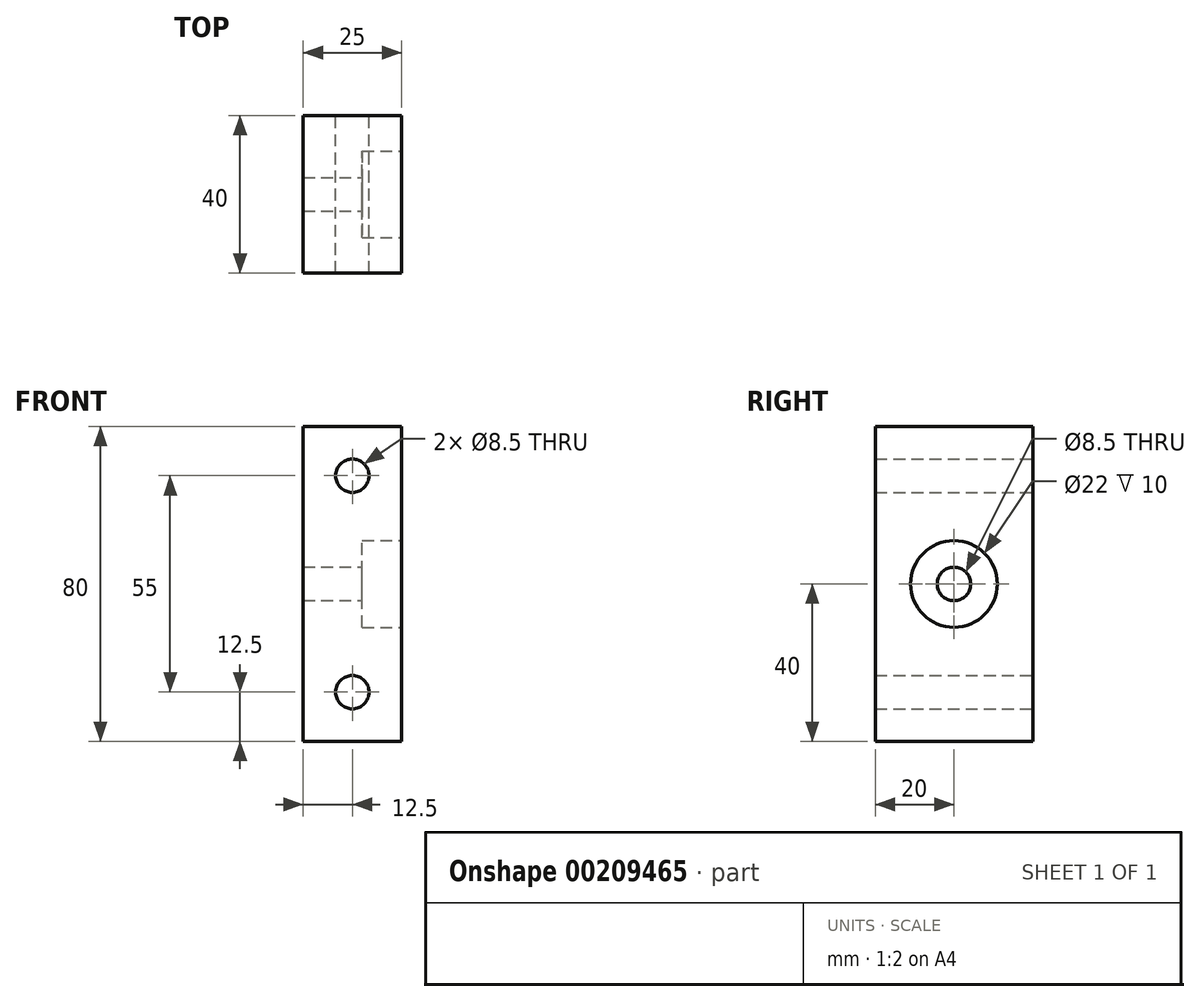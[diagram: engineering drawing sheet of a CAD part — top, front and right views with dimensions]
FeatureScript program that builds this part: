
annotation { "Feature Type Name" : "Feature", "Feature Type Description" : "" }
export const myFeature = defineFeature(function(context is Context, id is Id, definition is map)
    precondition{}
    {
        {
            var Q0;
            Q0=qCreatedBy(makeId("Front.planeOp"),FACE);
            var sketch = newSketch(context, id + "F0", { "sketchPlane" : qUnion([Q0])});
            skLineSegment(sketch, "E0.bottom", {"start": v(12.5, 40) * mm, "end": v(-12.5, 40) * mm});
            skLineSegment(sketch, "E0.top", {"start": v(12.5, -40) * mm, "end": v(-12.5, -40) * mm});
            skLineSegment(sketch, "E0.left", {"start": v(12.5, 40) * mm, "end": v(12.5, -40) * mm});
            skLineSegment(sketch, "E0.right", {"start": v(-12.5, 40) * mm, "end": v(-12.5, -40) * mm});
            skPoint(sketch, "E0.middle", {"position": v(0, 0) * mm});
            skCircle(sketch, "E1", {"center": v(0, 27.5) * mm, "radius": 4.25 * mm});
            skCircle(sketch, "E2", {"center": v(0, -27.5) * mm, "radius": 4.25 * mm});
            skSolve(sketch);
        }
        {
            var Q0;
            Q0 = qSketchRegion(id + "F0", true);
            extrude(context, id + "F1", {"entities" : qUnion([Q0]), "depth" : 20 * mm, "hasSecondDirection" : true, "secondDirectionOppositeDirection" : true, "secondDirectionDepth" : 20 * mm});
        }
        {
            var Q0;
            Q0=qCreatedBy(makeId("Right.planeOp"),FACE);
            var sketch = newSketch(context, id + "F2", { "sketchPlane" : qUnion([Q0])});
            skCircle(sketch, "E3", {"center": v(0, 0) * mm, "radius": 4.25 * mm});
            skSolve(sketch);
        }
        {
            var Q0;
            Q0 = qSketchRegion(id + "F2", true);
            extrude(context, id + "F3", {"entities" : qUnion([Q0]), "operationType" : NewBodyOperationType.REMOVE, "endBound" : BoundingType.UP_TO_NEXT, "oppositeDirection" : true, "depth" : 25 * mm});
        }
        {
            var Q0;
            Q0=makeQuery(id+"F1.opExtrude","SWEPT_FACE",FACE,{"disambiguationData":[OSD([sQuery(id+"F0.wireOp",EDGE,"E0.left")])]});
            var sketch = newSketch(context, id + "F4", { "sketchPlane" : qUnion([Q0])});
            skCircle(sketch, "E4", {"center": v(0, 0) * mm, "radius": 11 * mm});
            skSolve(sketch);
        }
        {
            var Q0;
            Q0 = qSketchRegion(id + "F4", true);
            extrude(context, id + "F5", {"entities" : qUnion([Q0]), "operationType" : NewBodyOperationType.REMOVE, "oppositeDirection" : true, "depth" : 10 * mm});
        }
        {
            var Q0;
            Q0=makeQuery(id+"F1.opExtrude","SWEPT_FACE",FACE,{"disambiguationData":[OSD([sQuery(id+"F0.wireOp",EDGE,"E0.left")])]});
            var sketch = newSketch(context, id + "F6", { "sketchPlane" : qUnion([Q0])});
            skCircle(sketch, "E5", {"center": v(0, 0) * mm, "radius": 4.25 * mm});
            skSolve(sketch);
        }
        {
            var Q0;
            Q0 = qSketchRegion(id + "F6", true);
            extrude(context, id + "F7", {"entities" : qUnion([Q0]), "operationType" : NewBodyOperationType.REMOVE, "oppositeDirection" : true, "depth" : 25 * mm});
        }
    });
